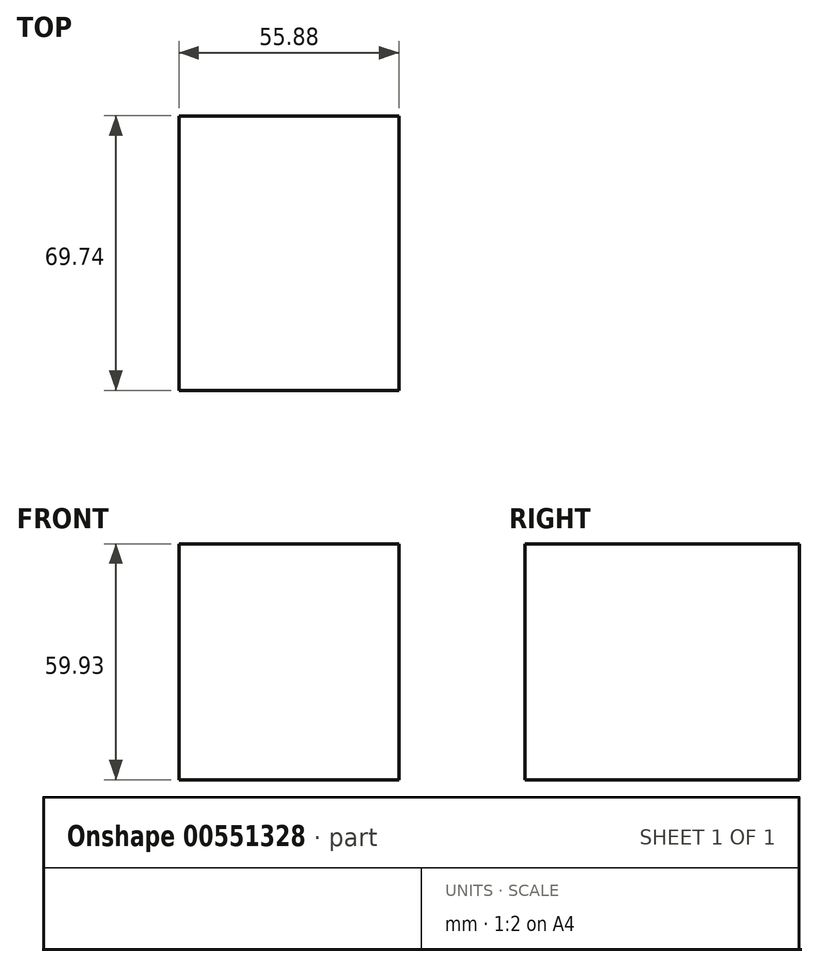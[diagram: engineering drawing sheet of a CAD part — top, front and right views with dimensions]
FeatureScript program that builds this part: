
annotation { "Feature Type Name" : "Feature", "Feature Type Description" : "" }
export const myFeature = defineFeature(function(context is Context, id is Id, definition is map)
    precondition{}
    {
        {
            var Q0;
            Q0=qCreatedBy(makeId("Right.planeOp"),FACE);
            var sketch = newSketch(context, id + "F0", { "sketchPlane" : qUnion([Q0])});
            skLineSegment(sketch, "E0.bottom", {"start": v(-31.43, 40.63) * mm, "end": v(38.3, 40.63) * mm});
            skLineSegment(sketch, "E0.top", {"start": v(-31.43, -19.3) * mm, "end": v(38.3, -19.3) * mm});
            skLineSegment(sketch, "E0.left", {"start": v(-31.43, 40.63) * mm, "end": v(-31.43, -19.3) * mm});
            skLineSegment(sketch, "E0.right", {"start": v(38.3, 40.63) * mm, "end": v(38.3, -19.3) * mm});
            skSolve(sketch);
        }
        {
            var Q0;
            Q0=makeQuery(id+"F0.imprint","IMPRINT",FACE,{"disambiguationData":[TD([[makeQuery(id+"F0.imprint","IMPRINT",EDGE,{"derivedFrom":sQuery(id+"F0.wireOp",EDGE,"E0.bottom")}),-1.0]])]});
            extrude(context, id + "F1", {"entities" : qUnion([Q0]), "depth" : 55.88 * mm, "offsetDistance" : 25.4 * mm});
        }
    });
